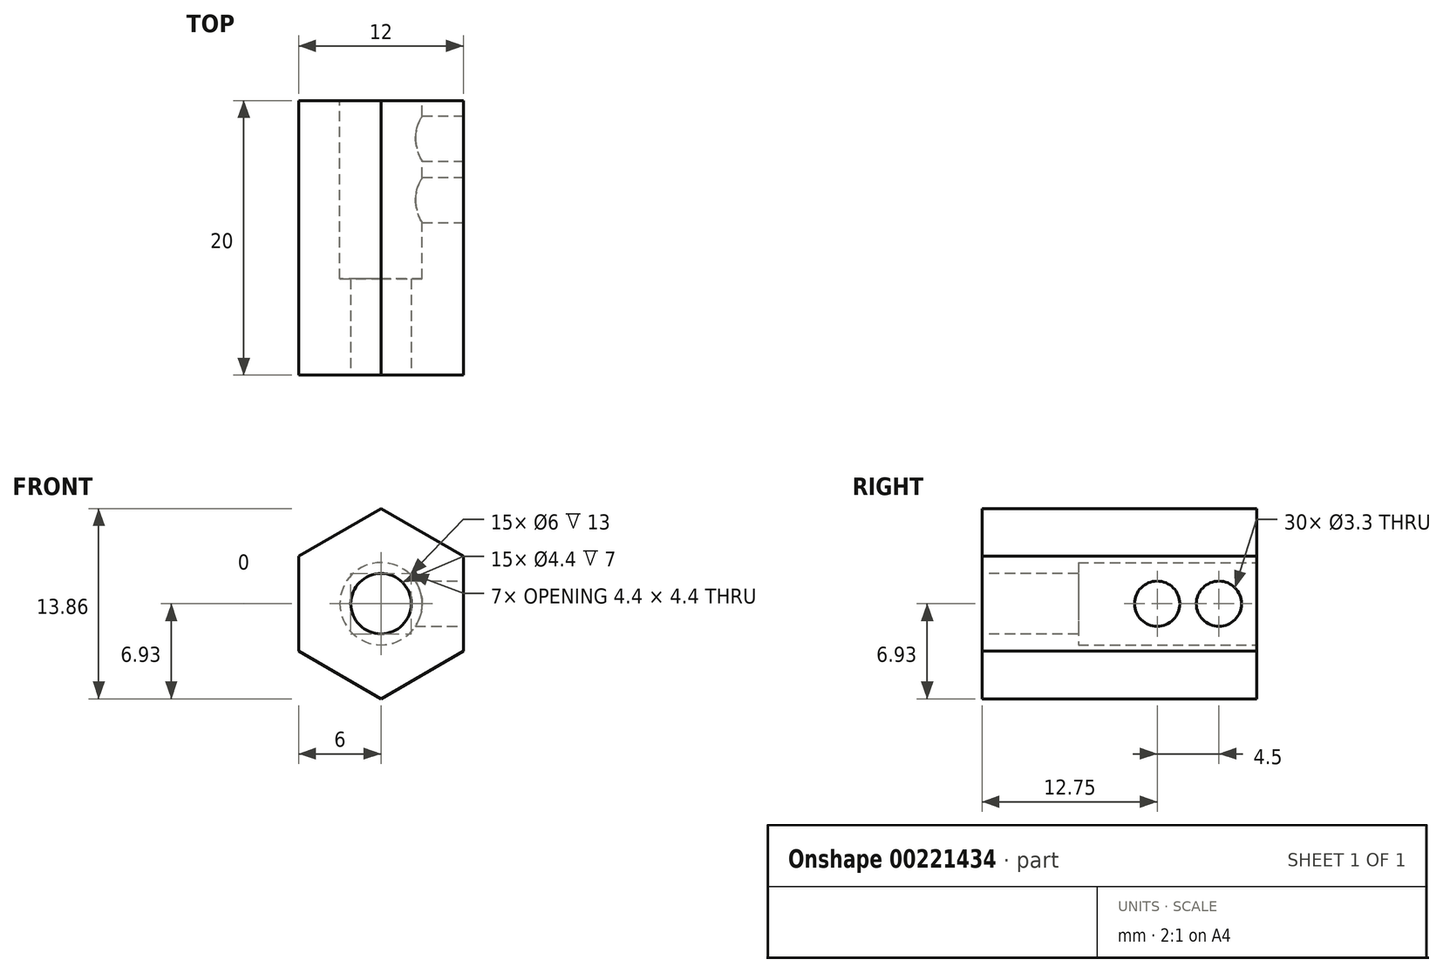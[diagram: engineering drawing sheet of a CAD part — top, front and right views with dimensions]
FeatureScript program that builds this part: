
annotation { "Feature Type Name" : "Feature", "Feature Type Description" : "" }
export const myFeature = defineFeature(function(context is Context, id is Id, definition is map)
    precondition{}
    {
        {
            var Q0;
            Q0=qCreatedBy(makeId("Front.planeOp"),FACE);
            var sketch = newSketch(context, id + "F0", { "sketchPlane" : qUnion([Q0])});
            skCircle(sketch, "E0.cCircle", {"center": v(0, 0) * mm, "radius": 6 * mm, "construction": true});
            skLineSegment(sketch, "E0.0", {"start": v(6, 3.46) * mm, "end": v(6, -3.46) * mm});
            skLineSegment(sketch, "E0.1", {"start": v(6, -3.46) * mm, "end": v(0, -6.93) * mm});
            skLineSegment(sketch, "E0.2", {"start": v(0, -6.93) * mm, "end": v(-6, -3.46) * mm});
            skLineSegment(sketch, "E0.3", {"start": v(-6, -3.46) * mm, "end": v(-6, 3.46) * mm});
            skLineSegment(sketch, "E0.4", {"start": v(-6, 3.46) * mm, "end": v(0, 6.93) * mm});
            skLineSegment(sketch, "E0.5", {"start": v(0, 6.93) * mm, "end": v(6, 3.46) * mm});
            skPoint(sketch, "E0.0.midPoint", {"position": v(6, 0) * mm});
            skSolve(sketch);
        }
        {
            var Q0;
            Q0 = qSketchRegion(id + "F0", true);
            extrude(context, id + "F1", {"entities" : qUnion([Q0]), "depth" : 20 * mm});
        }
        {
            var Q0;
            Q0=makeQuery(id+"F1.opExtrude","CAP_FACE",FACE,{"disambiguationData":[OSD([sQuery(id+"F0.wireOp",EDGE,"E0.0"),sQuery(id+"F0.wireOp",EDGE,"E0.1"),sQuery(id+"F0.wireOp",EDGE,"E0.2"),sQuery(id+"F0.wireOp",EDGE,"E0.3"),sQuery(id+"F0.wireOp",EDGE,"E0.4"),sQuery(id+"F0.wireOp",EDGE,"E0.5")])],"isStart":true});
            var sketch = newSketch(context, id + "F2", { "sketchPlane" : qUnion([Q0])});
            skCircle(sketch, "E1", {"center": v(0, 0) * mm, "radius": 3 * mm});
            skSolve(sketch);
        }
        {
            var Q0;
            Q0 = qSketchRegion(id + "F2", true);
            extrude(context, id + "F3", {"entities" : qUnion([Q0]), "operationType" : NewBodyOperationType.REMOVE, "oppositeDirection" : true, "depth" : 13 * mm});
        }
        {
            var Q0;
            Q0=makeQuery(id+"F1.opExtrude","CAP_FACE",FACE,{"disambiguationData":[OSD([sQuery(id+"F0.wireOp",EDGE,"E0.0"),sQuery(id+"F0.wireOp",EDGE,"E0.1"),sQuery(id+"F0.wireOp",EDGE,"E0.2"),sQuery(id+"F0.wireOp",EDGE,"E0.3"),sQuery(id+"F0.wireOp",EDGE,"E0.4"),sQuery(id+"F0.wireOp",EDGE,"E0.5")])],"isStart":false});
            var sketch = newSketch(context, id + "F4", { "sketchPlane" : qUnion([Q0])});
            skPoint(sketch, "E2", {"position": v(0, 0) * mm});
            skSolve(sketch);
        }
        {
            var Q0;
            Q0=sQuery(id+"F4.wireOp",VERTEX,"E2");
            var Q1;
            Q1=makeQuery(id+"F1.opExtrude","SWEPT_BODY",BODY,{"disambiguationData":[OSD([sQuery(id+"F0.wireOp",EDGE,"E0.0"),sQuery(id+"F0.wireOp",EDGE,"E0.1"),sQuery(id+"F0.wireOp",EDGE,"E0.2"),sQuery(id+"F0.wireOp",EDGE,"E0.3"),sQuery(id+"F0.wireOp",EDGE,"E0.4"),sQuery(id+"F0.wireOp",EDGE,"E0.5")])]});
            hole(context, id + "F5", {"style" : HoleStyle.SIMPLE, "endStyle" : HoleEndStyle.THROUGH, "standardTappedOrClearance" : lookupTablePath({ "standard" : "ISO", "fit" : "Normal", "size" : "M4", "type" : "Clearance" }), "standardBlindInLast" : lookupTablePath({ "fit" : "Standard", "standard" : "ISO", "size" : "M4", "type" : "Clearance" }), "holeDiameter" : 4.4 * mm, "locations" : qUnion([Q0]), "scope" : qUnion([Q1]), "isTappedThrough" : true});
        }
        {
            var Q0;
            Q0=makeQuery(id+"F1.opExtrude","SWEPT_FACE",FACE,{"disambiguationData":[OSD([sQuery(id+"F0.wireOp",EDGE,"E0.0")])]});
            var sketch = newSketch(context, id + "F6", { "sketchPlane" : qUnion([Q0])});
            skPoint(sketch, "E3", {"position": v(-2.75, 0) * mm});
            skPoint(sketch, "E4", {"position": v(-7.25, 0) * mm});
            skSolve(sketch);
        }
        {
            var Q0;
            Q0=sQuery(id+"F6.wireOp",VERTEX,"E3");
            var Q1;
            Q1=sQuery(id+"F6.wireOp",VERTEX,"E4");
            var Q2;
            Q2=makeQuery(id+"F1.opExtrude","SWEPT_BODY",BODY,{"disambiguationData":[OSD([sQuery(id+"F0.wireOp",EDGE,"E0.0"),sQuery(id+"F0.wireOp",EDGE,"E0.1"),sQuery(id+"F0.wireOp",EDGE,"E0.2"),sQuery(id+"F0.wireOp",EDGE,"E0.3"),sQuery(id+"F0.wireOp",EDGE,"E0.4"),sQuery(id+"F0.wireOp",EDGE,"E0.5")])]});
            hole(context, id + "F7", {"style" : HoleStyle.SIMPLE, "endStyle" : HoleEndStyle.BLIND, "standardTappedOrClearance" : lookupTablePath({ "standard" : "ISO", "fit" : "Normal", "size" : "M3", "type" : "Clearance" }), "standardBlindInLast" : lookupTablePath({ "fit" : "Standard", "standard" : "ISO", "size" : "M3", "type" : "Clearance" }), "holeDiameter" : 3.3 * mm, "holeDepth" : 6 * mm, "locations" : qUnion([Q0, Q1]), "scope" : qUnion([Q2])});
        }
    });
